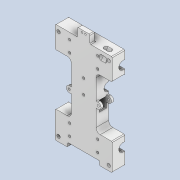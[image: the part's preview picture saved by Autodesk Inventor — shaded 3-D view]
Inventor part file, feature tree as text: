
AUTODESK INVENTOR PART (.ipt)
format: ipt  version: 2020 (Build 240168000, 168)  size: 408,576 bytes
history: native  units: mm
features: sketch x13, extrude x10, mirror x4, fillet x4, hole x4, other x4, reference x2, plane x1
ambient origin geometry x8: Origin, YZ Plane, XZ Plane, XY Plane, X Axis, Y Axis, Z Axis, Center Point
bodies: Solid1 (feature_tree)
feature tree (42):
  extrude  "Extrusion1"  Depth=136.0mm
  extrude  "Extrusion2"  Depth=30.0mm
  extrude  "Extrusion3"  Depth=30.0mm
  extrude  "Extrusion4"  Depth=11.75mm
  mirror  "Mirror1"
  extrude  "Extrusion5"  Depth=8.0mm
  extrude  "Extrusion6"  Depth=8.0mm
  fillet  "Fillet2"  [1 undecoded]
  mirror  "Mirror2"
  hole  "Hole1"  [1 undecoded]
  mirror  "Mirror3"
  mirror  "Mirror4"
  hole  "Hole2"  [1 undecoded]
  extrude  "Extrusion7"  Depth=15.0mm
  extrude  "Extrusion9"  Depth=20.0mm
  hole  "Hole3"  [1 undecoded]
  fillet  "Fillet3"  Radius=12.0mm
  extrude  "Extrusion10"  Depth=5.0mm
  fillet  "Fillet4"  Radius=5.0mm
  fillet  "Fillet5"  Radius=5.0mm
  hole  "Hole5"  [1 undecoded]
  plane  "Work Plane1"
  extrude  "Extrusion11"  Depth=8.0mm
  sketch  "Sketch1"  dims[d0=230.0mm d1=136.0mm]
  sketch  "Sketch3"  dims[d2=30.0mm d3=0.0mm d4=30.0mm]
  reference  "Reference8"
  sketch  "Sketch5"  dims[d6=19.5mm d7=30.0mm]
  sketch  "Sketch6"  dims[d8=0.0mm d9=0.0mm d10=11.75mm]
  sketch  "Sketch8"  dims[d11=8.0mm d12=8.0mm]
  sketch  "Sketch10"  dims[d19=4.5mm d20=1.5mm]
  sketch  "Sketch11"  dims[d21=29.0mm d22=15.0mm]
  sketch  "Sketch13"  dims[d23=12.5mm d24=15.0mm]
  sketch  "Sketch14"  dims[d25=47.0mm d26=0.0mm d28=20.0mm]
  sketch  "Sketch15"  dims[d29=15.0mm d31=3.0mm d32=12.0mm d33=0.0mm]
  sketch  "Sketch17"  dims[d38=5.0mm d39=5.0mm d40=5.0mm d41=5.0mm]
  reference  "Reference13"
  sketch  "Sketch19"  dims[d42=0.0mm d43=0.0mm d44=7.5mm d50=5.5mm d51=6.0mm d52=9.0mm d53=2.0mm d54=90.0deg d55=8.0mm d56=20.594885mm d59=15.0mm d60=10.0mm d61=7.5mm d62=7.5mm d63=5.5mm d64=6.0mm d65=9.0mm d66=2.0mm d67=90.0deg d68=8.0mm d69=20.594885mm d70=34.5mm d74=0.0mm d75=0.0mm d78=2.5mm d79=0.0mm d80=25.0mm d81=112.5mm d86=20.0mm d87=30.0mm d88=10.0mm d89=0.0mm d90=8.0mm d91=4.0mm d92=4.0mm d93=6.0mm d94=4.0mm d95=2.0mm d96=90.0deg d97=8.0mm d98=20.594885mm d99=2.0mm d100=30.0mm d101=10.0mm d102=10.0mm d103=0.0mm d111=2.0mm d112=10.0mm d113=2.459mm d114=6.0mm d115=4.0mm d116=2.0mm d117=90.0deg d118=8.8mm d119=20.594885mm d120=10.0mm d121=8.0mm d122=21.5mm d124=5.0mm d125=16.37mm d126=0.0mm d127=5.0mm]
  parser-record x1  (decoder bookkeeping rows leaked as tree rows — omitted from the tree; the rows remain in map.json)
  other  "0008-10-02 X Axis.iam"
  other  "0008-10-1009 LM10uu.ipt:7"
  sketch  "Sketch9"  dims[d13=8.0mm d14=1.75mm d15=0.0mm d16=0.0mm]
  other  "0008-20-1003 Switch:1"
note: 5 required parameter values undecoded (feature->parameter linkage not recoverable at this tier; creation-order binding heuristic only, values carry confidence <= 0.55)
note: 1 file-system path scrubbed to <path> (originals preserved in map.json)
